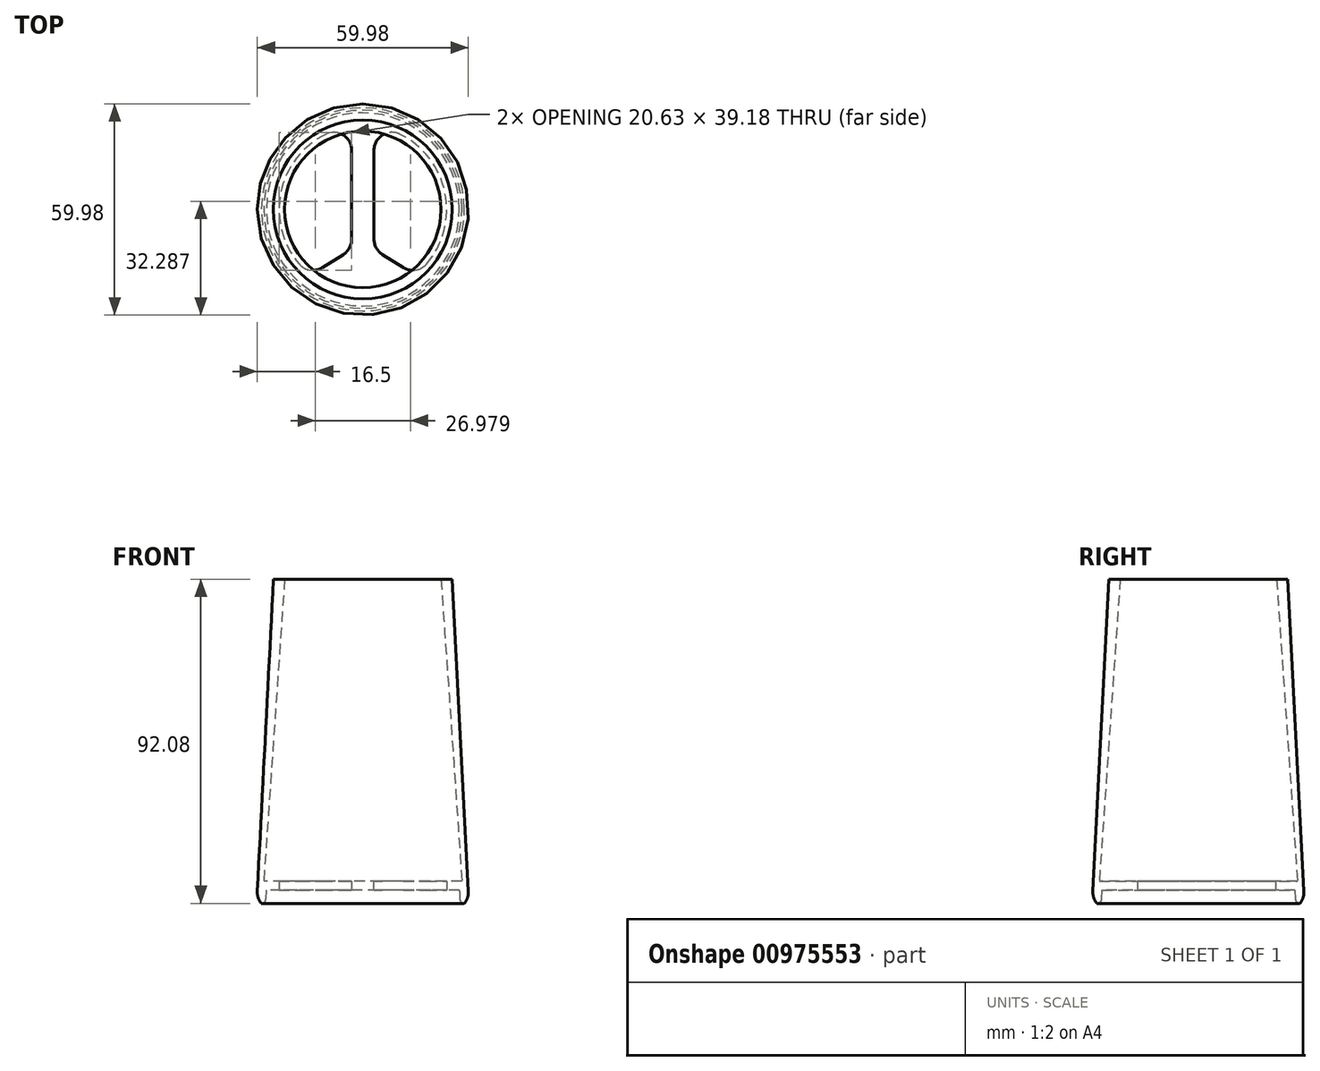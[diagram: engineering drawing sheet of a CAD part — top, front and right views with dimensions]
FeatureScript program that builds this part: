
annotation { "Feature Type Name" : "Feature", "Feature Type Description" : "" }
export const myFeature = defineFeature(function(context is Context, id is Id, definition is map)
    precondition{}
    {
        {
            var Q0;
            Q0=qCreatedBy(makeId("Top.planeOp"),FACE);
            var sketch = newSketch(context, id + "F0", { "sketchPlane" : qUnion([Q0])});
            skCircle(sketch, "E0", {"center": v(0, 0) * mm, "radius": 30.16 * mm});
            skCircle(sketch, "E1", {"center": v(0, 0) * mm, "radius": 28.58 * mm});
            skLineSegment(sketch, "E2.0", {"start": v(-3.17, 28.4) * mm, "end": v(-3.17, -28.4) * mm});
            skLineSegment(sketch, "E3.0", {"start": v(3.17, 28.4) * mm, "end": v(3.17, -28.4) * mm});
            skLineSegment(sketch, "E4", {"start": v(-3.17, -11.33) * mm, "end": v(-14.85, -18.61) * mm});
            skCircle(sketch, "E5", {"center": v(0, 0) * mm, "radius": 23.81 * mm});
            skLineSegment(sketch, "E6.MirrorCS", {"start": v(3.17, -11.33) * mm, "end": v(14.85, -18.61) * mm});
            skSolve(sketch);
        }
        {
            var Q0;
            Q0=qCreatedBy(makeId("Front.planeOp"),FACE);
            var sketch = newSketch(context, id + "F1", { "sketchPlane" : qUnion([Q0])});
            skLineSegment(sketch, "E7", {"start": v(0, 0) * mm, "end": v(0, 92.08) * mm});
            skLineSegment(sketch, "E8", {"start": v(0, 0) * mm, "end": v(-30.16, 0) * mm});
            skLineSegment(sketch, "E9", {"start": v(0, 92.08) * mm, "end": v(-25.4, 92.08) * mm});
            skLineSegment(sketch, "E10", {"start": v(-25.4, 92.07) * mm, "end": v(-30.16, 0) * mm});
            skSolve(sketch);
        }
        {
            var Q0;
            Q0=makeQuery(id+"F1.imprint","IMPRINT",FACE,{"disambiguationData":[TD([[makeQuery(id+"F1.imprint","IMPRINT",EDGE,{"derivedFrom":sQuery(id+"F1.wireOp",EDGE,"E7")}),1.0]])]});
            var Q1;
            Q1=sQuery(id+"F1.wireOp",EDGE,"E7");
            revolve(context, id + "F2", {"surfaceOperationType" : NewSurfaceOperationType.NEW, "entities" : qUnion([Q0]), "axis" : qUnion([Q1]), "revolveType" : RevolveType.FULL});
        }
        {
            var Q0;
            Q0=qCreatedBy(makeId("Front.planeOp"),FACE);
            var sketch = newSketch(context, id + "F3", { "sketchPlane" : qUnion([Q0])});
            skLineSegment(sketch, "E11", {"start": v(0, 0) * mm, "end": v(28.58, 0) * mm});
            skLineSegment(sketch, "E12", {"start": v(0, 0) * mm, "end": v(0, 92.08) * mm});
            skLineSegment(sketch, "E13", {"start": v(0, 92.08) * mm, "end": v(22.23, 92.08) * mm});
            skLineSegment(sketch, "E14", {"start": v(22.23, 92.08) * mm, "end": v(28.58, 0) * mm});
            skSolve(sketch);
        }
        {
            var Q0;
            Q0=makeQuery(id+"F3.imprint","IMPRINT",FACE,{"disambiguationData":[TD([[makeQuery(id+"F3.imprint","IMPRINT",EDGE,{"derivedFrom":sQuery(id+"F3.wireOp",EDGE,"E11")}),1.0]])]});
            var Q1;
            Q1=sQuery(id+"F3.wireOp",EDGE,"E12");
            revolve(context, id + "F4", {"operationType" : NewBodyOperationType.REMOVE, "surfaceOperationType" : NewSurfaceOperationType.NEW, "entities" : qUnion([Q0]), "axis" : qUnion([Q1]), "revolveType" : RevolveType.FULL, "oppositeDirection" : true});
        }
        {
            var Q0;
            {var subQ0=sQuery(id+"F0.wireOp",EDGE,"E4");Q0=makeQuery(id+"F0.imprint","IMPRINT",FACE,{"disambiguationData":[TD([[makeQuery(id+"F0.imprint","IMPRINT",EDGE,{"derivedFrom":subQ0}),-1.0]])]});}
            var Q1;
            {var subQ0=sQuery(id+"F0.wireOp",EDGE,"E6.MirrorCS");Q1=makeQuery(id+"F0.imprint","IMPRINT",FACE,{"disambiguationData":[TD([[makeQuery(id+"F0.imprint","IMPRINT",EDGE,{"derivedFrom":subQ0}),1.0]])]});}
            var Q2;
            {var subQ4=sQuery(id+"F0.wireOp",EDGE,"E2.0");var subQ5=makeQuery(id+"F0.imprint","INTERSECT",VERTEX,{"derivedFrom":[subQ4,sQuery(id+"F0.wireOp",EDGE,"E4")]});Q2=makeQuery(id+"F0.imprint","IMPRINT",FACE,{"disambiguationData":[TD([[makeQuery(id+"F0.imprint","IMPRINT",EDGE,{"disambiguationData":[TD([[subQ5,1.0]])],"derivedFrom":subQ4}),1.0]])]});}
            var Q3;
            {var subQ0=sQuery(id+"F0.wireOp",EDGE,"E6.MirrorCS");Q3=makeQuery(id+"F0.imprint","IMPRINT",FACE,{"disambiguationData":[TD([[makeQuery(id+"F0.imprint","IMPRINT",EDGE,{"derivedFrom":subQ0}),-1.0]])]});}
            var Q4;
            {var subQ0=sQuery(id+"F0.wireOp",EDGE,"E4");Q4=makeQuery(id+"F0.imprint","IMPRINT",FACE,{"disambiguationData":[TD([[makeQuery(id+"F0.imprint","IMPRINT",EDGE,{"derivedFrom":subQ0}),1.0]])]});}
            var Q5;
            {var subQ0=sQuery(id+"F0.wireOp",EDGE,"E2.0");var subQ1=sQuery(id+"F0.wireOp",EDGE,"E1");var subQ7=makeQuery(id+"F0.imprint","INTERSECT",VERTEX,{"disambiguationData":[OD(0.0)],"derivedFrom":[subQ1,subQ0]});Q5=makeQuery(id+"F0.imprint","IMPRINT",FACE,{"disambiguationData":[TD([[makeQuery(id+"F0.imprint","IMPRINT",EDGE,{"disambiguationData":[TD([[subQ7,-1.0]])],"derivedFrom":subQ1}),1.0]])]});}
            var Q6;
            {var subQ2=sQuery(id+"F0.wireOp",EDGE,"E3.0");var subQ4=sQuery(id+"F0.wireOp",EDGE,"E1");var subQ6=makeQuery(id+"F0.imprint","INTERSECT",VERTEX,{"disambiguationData":[OD(0.0)],"derivedFrom":[subQ4,subQ2]});Q6=makeQuery(id+"F0.imprint","IMPRINT",FACE,{"disambiguationData":[TD([[makeQuery(id+"F0.imprint","IMPRINT",EDGE,{"disambiguationData":[TD([[subQ6,1.0]])],"derivedFrom":subQ4}),1.0]])]});}
            var Q7;
            {var subQ0=sQuery(id+"F0.wireOp",EDGE,"E2.0");var subQ1=sQuery(id+"F0.wireOp",EDGE,"E1");var subQ2=makeQuery(id+"F0.imprint","INTERSECT",VERTEX,{"disambiguationData":[OD(1.0)],"derivedFrom":[subQ1,subQ0]});Q7=makeQuery(id+"F0.imprint","IMPRINT",FACE,{"disambiguationData":[TD([[makeQuery(id+"F0.imprint","IMPRINT",EDGE,{"disambiguationData":[TD([[subQ2,-1.0]])],"derivedFrom":subQ1}),1.0]])]});}
            var Q8;
            {var subQ0=sQuery(id+"F0.wireOp",EDGE,"E2.0");var subQ1=sQuery(id+"F0.wireOp",EDGE,"E1");var subQ2=makeQuery(id+"F0.imprint","INTERSECT",VERTEX,{"disambiguationData":[OD(0.0)],"derivedFrom":[subQ1,subQ0]});Q8=makeQuery(id+"F0.imprint","IMPRINT",FACE,{"disambiguationData":[TD([[makeQuery(id+"F0.imprint","IMPRINT",EDGE,{"disambiguationData":[TD([[subQ2,1.0]])],"derivedFrom":subQ1}),1.0]])]});}
            extrude(context, id + "F5", {"entities" : qUnion([Q0, Q1, Q2, Q3, Q4, Q5, Q6, Q7, Q8]), "operationType" : NewBodyOperationType.ADD, "depth" : 6.35 * mm, "offsetDistance" : 25.4 * mm});
        }
        {
            var Q0;
            Q0=makeQuery(id+"F5.boolean.opBoolean","MERGE",FACE,{"derivedFrom":[makeQuery(id+"F2.opRevolve","SWEPT_FACE",FACE,{"disambiguationData":[OSD([sQuery(id+"F1.wireOp",EDGE,"E8")])]}),makeQuery(id+"F5.opExtrude","CAP_FACE",FACE,{"disambiguationData":[OSD([sQuery(id+"F0.wireOp",EDGE,"E1")])],"isStart":true})]});
            shell(context, id + "F6", {"entities" : qUnion([Q0]), "thickness" : 2.54 * mm});
        }
        {
            var Q0;
            {var subQ0=sQuery(id+"F0.wireOp",EDGE,"E4");Q0=makeQuery(id+"F0.imprint","IMPRINT",FACE,{"disambiguationData":[TD([[makeQuery(id+"F0.imprint","IMPRINT",EDGE,{"derivedFrom":subQ0}),-1.0]])]});}
            var Q1;
            {var subQ0=sQuery(id+"F0.wireOp",EDGE,"E6.MirrorCS");Q1=makeQuery(id+"F0.imprint","IMPRINT",FACE,{"disambiguationData":[TD([[makeQuery(id+"F0.imprint","IMPRINT",EDGE,{"derivedFrom":subQ0}),1.0]])]});}
            extrude(context, id + "F7", {"entities" : qUnion([Q0, Q1]), "operationType" : NewBodyOperationType.REMOVE, "depth" : 25.4 * mm, "offsetDistance" : 25.4 * mm});
        }
        {
            var Q0;
            Q0=makeQuery(id+"F7.boolean.opBoolean","COPY",EDGE,{"derivedFrom":makeQuery(id+"F7.opExtrude","SWEPT_EDGE",EDGE,{"disambiguationData":[OSD([sQuery(id+"F0.wireOp",EDGE,"E5"),sQuery(id+"F0.wireOp",EDGE,"E6.MirrorCS")])]})});
            var Q1;
            Q1=makeQuery(id+"F7.boolean.opBoolean","COPY",EDGE,{"derivedFrom":makeQuery(id+"F7.opExtrude","SWEPT_EDGE",EDGE,{"disambiguationData":[OSD([sQuery(id+"F0.wireOp",EDGE,"E4"),sQuery(id+"F0.wireOp",EDGE,"E5")])]})});
            var Q2;
            Q2=makeQuery(id+"F7.boolean.opBoolean","COPY",EDGE,{"derivedFrom":makeQuery(id+"F7.opExtrude","SWEPT_EDGE",EDGE,{"disambiguationData":[OSD([sQuery(id+"F0.wireOp",EDGE,"E2.0"),sQuery(id+"F0.wireOp",EDGE,"E4")])]})});
            var Q3;
            Q3=makeQuery(id+"F7.boolean.opBoolean","COPY",EDGE,{"derivedFrom":makeQuery(id+"F7.opExtrude","SWEPT_EDGE",EDGE,{"disambiguationData":[OSD([sQuery(id+"F0.wireOp",EDGE,"E3.0"),sQuery(id+"F0.wireOp",EDGE,"E6.MirrorCS")])]})});
            var Q4;
            Q4=makeQuery(id+"F7.boolean.opBoolean","COPY",EDGE,{"derivedFrom":makeQuery(id+"F7.opExtrude","SWEPT_EDGE",EDGE,{"disambiguationData":[OSD([sQuery(id+"F0.wireOp",EDGE,"E3.0"),sQuery(id+"F0.wireOp",EDGE,"E5")])]})});
            var Q5;
            Q5=makeQuery(id+"F7.boolean.opBoolean","COPY",EDGE,{"derivedFrom":makeQuery(id+"F7.opExtrude","SWEPT_EDGE",EDGE,{"disambiguationData":[OSD([sQuery(id+"F0.wireOp",EDGE,"E2.0"),sQuery(id+"F0.wireOp",EDGE,"E5")])]})});
            fillet(context, id + "F8", {"entities" : qUnion([Q0, Q1, Q2, Q3, Q4, Q5]), "radius" : 5.08 * mm, "tangentPropagation" : true, "allowEdgeOverflow" : false});
        }
        {
            var Q0;
            Q0=makeQuery(id+"F6.opShell","OFFSET_EDGE",EDGE,{"disambiguationData":[OSD([sQuery(id+"F1.wireOp",EDGE,"E8"),sQuery(id+"F1.wireOp",EDGE,"E10")])]});
            fillet(context, id + "F9", {"entities" : qUnion([Q0]), "radius" : 1.27 * mm, "tangentPropagation" : true, "allowEdgeOverflow" : false});
        }
        {
            var Q0;
            Q0=makeQuery(id+"F2.opRevolve","SWEPT_EDGE",EDGE,{"disambiguationData":[OSD([sQuery(id+"F1.wireOp",EDGE,"E8"),sQuery(id+"F1.wireOp",EDGE,"E10")])]});
            fillet(context, id + "F10", {"entities" : qUnion([Q0]), "radius" : 5.08 * mm, "tangentPropagation" : true, "allowEdgeOverflow" : false});
        }
    });
